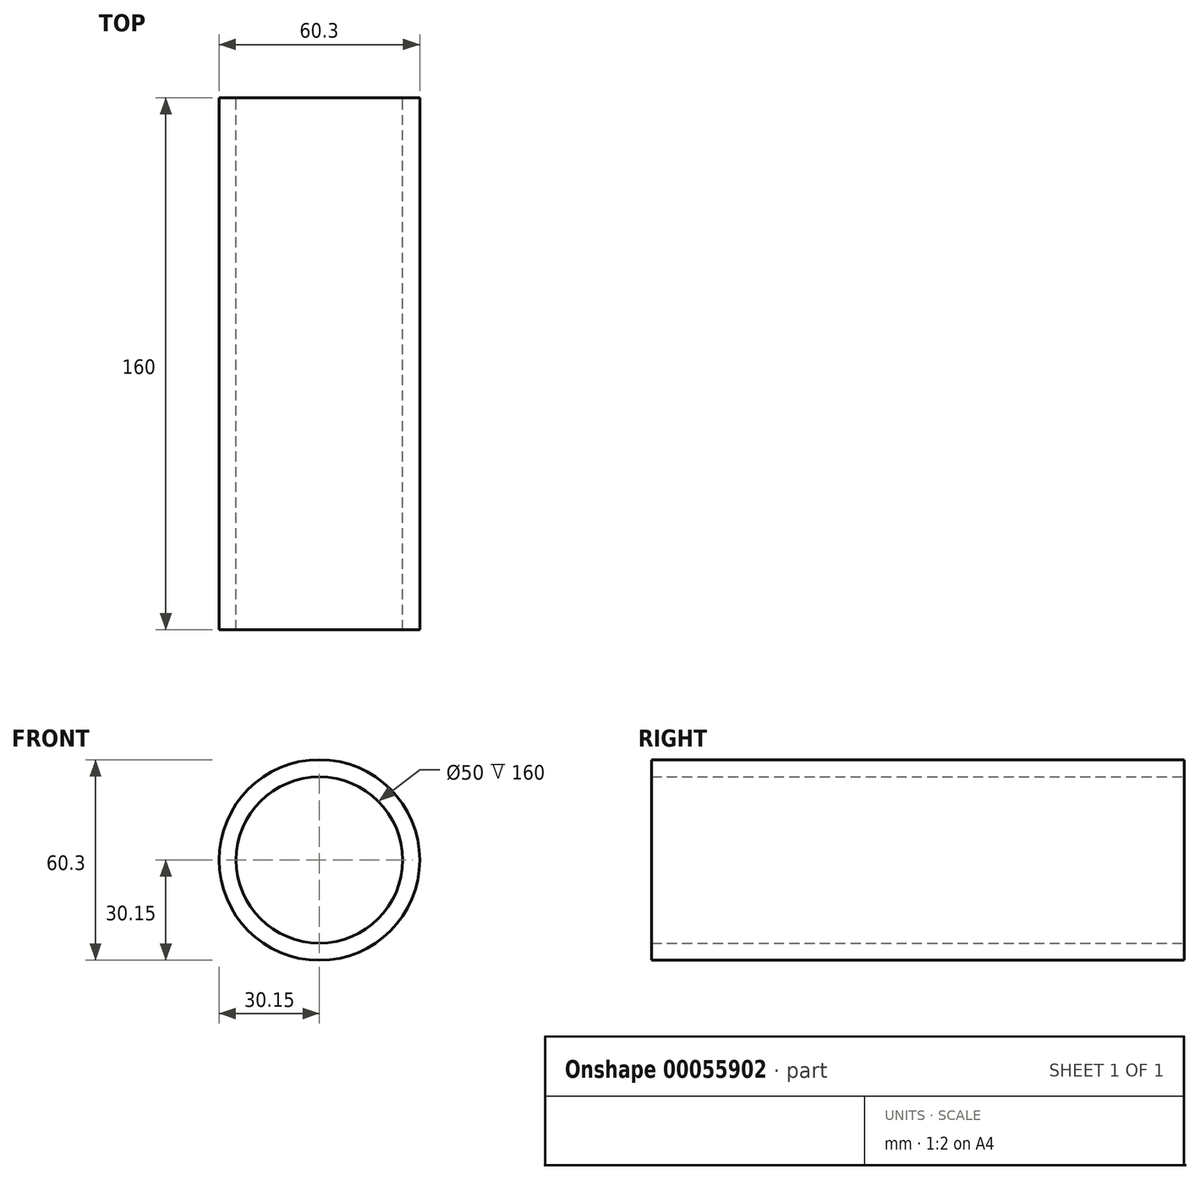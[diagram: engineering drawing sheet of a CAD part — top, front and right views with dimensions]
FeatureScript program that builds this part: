
annotation { "Feature Type Name" : "Feature", "Feature Type Description" : "" }
export const myFeature = defineFeature(function(context is Context, id is Id, definition is map)
    precondition{}
    {
        {
            var Q0;
            Q0=qCreatedBy(makeId("Front.planeOp"),FACE);
            var sketch = newSketch(context, id + "F0", { "sketchPlane" : qUnion([Q0])});
            skCircle(sketch, "E0", {"center": v(0, 0) * mm, "radius": 25 * mm});
            skCircle(sketch, "E1", {"center": v(0, 0) * mm, "radius": 30.15 * mm});
            skSolve(sketch);
        }
        {
            var Q0;
            Q0=makeQuery(id+"F0.imprint","IMPRINT",FACE,{"disambiguationData":[TD([[makeQuery(id+"F0.imprint","IMPRINT",EDGE,{"derivedFrom":sQuery(id+"F0.wireOp",EDGE,"E0")}),-1.0]])]});
            extrude(context, id + "F1", {"entities" : qUnion([Q0]), "depth" : 160 * mm});
        }
    });
